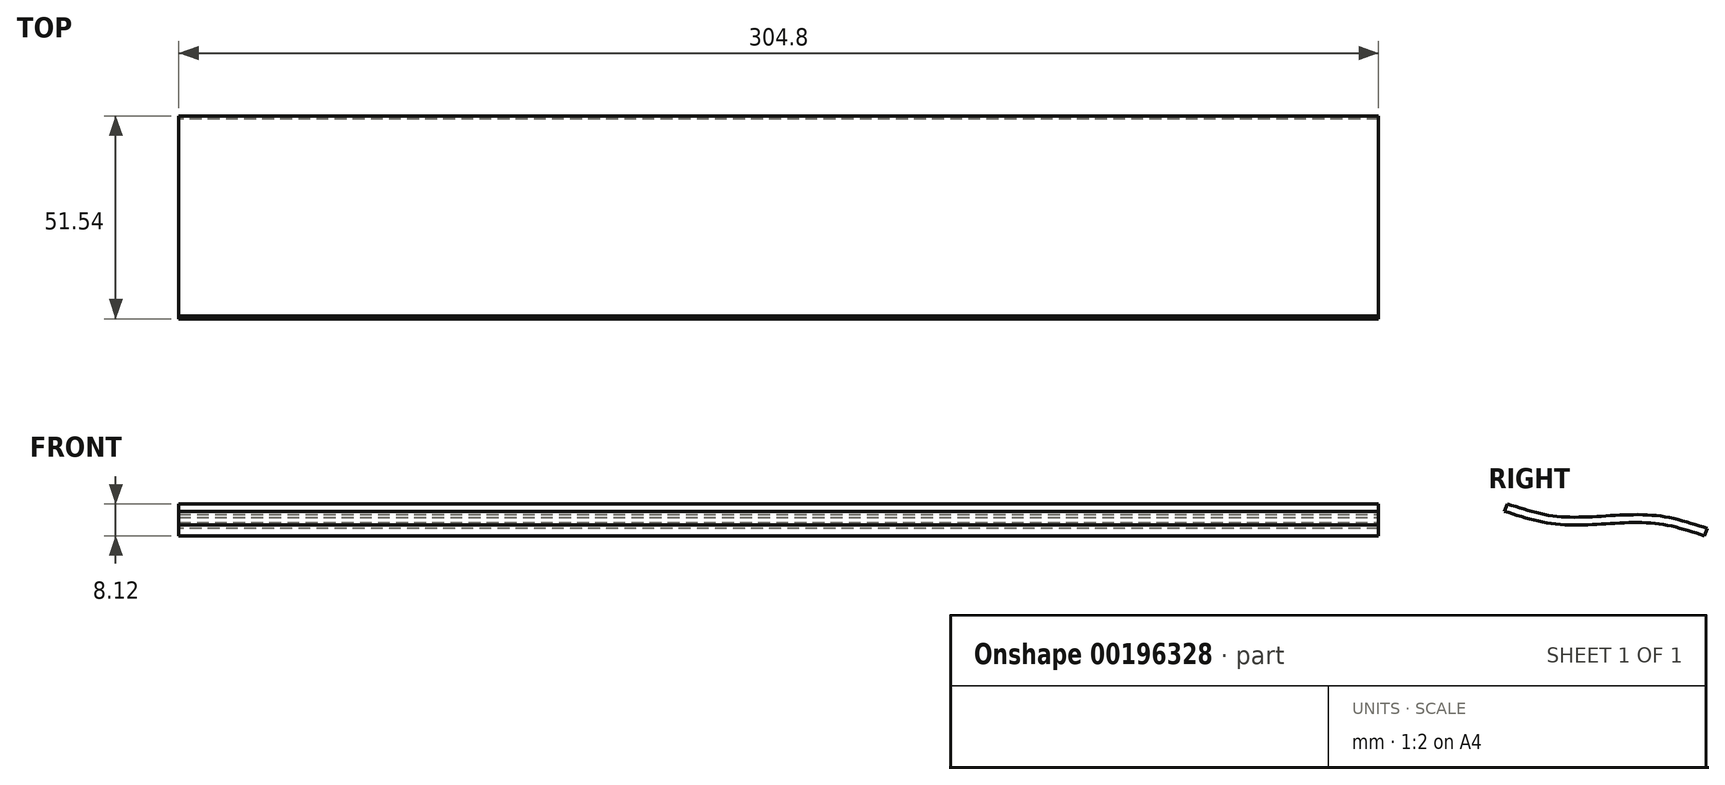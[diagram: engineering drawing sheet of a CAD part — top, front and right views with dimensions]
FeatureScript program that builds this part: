
annotation { "Feature Type Name" : "Feature", "Feature Type Description" : "" }
export const myFeature = defineFeature(function(context is Context, id is Id, definition is map)
    precondition{}
    {
        {
            var Q0;
            Q0=qCreatedBy(makeId("Front.planeOp"),FACE);
            var sketch = newSketch(context, id + "F0", { "sketchPlane" : qUnion([Q0])});
            skLineSegment(sketch, "E0.bottom", {"start": v(152.4, 1) * mm, "end": v(-152.4, 1) * mm});
            skLineSegment(sketch, "E0.top", {"start": v(152.4, -1) * mm, "end": v(-152.4, -1) * mm});
            skLineSegment(sketch, "E0.left", {"start": v(152.4, 1) * mm, "end": v(152.4, -1) * mm});
            skLineSegment(sketch, "E0.right", {"start": v(-152.4, 1) * mm, "end": v(-152.4, -1) * mm});
            skPoint(sketch, "E0.middle", {"position": v(0, 0) * mm});
            skSolve(sketch);
        }
        {
            var Q0;
            Q0=qCreatedBy(makeId("Right.planeOp"),FACE);
            var sketch = newSketch(context, id + "F1", { "sketchPlane" : qUnion([Q0])});
            skFitSpline(sketch, "E1", {"points": [v(0, 0) * mm, v(-13.38, 0) * mm, v(-25.4, 3.13) * mm], "startDerivative": vector(-26.73, -1.62) * mm, "endDerivative": vector(-24.06, 7.94) * mm});
            skLineSegment(sketch, "E2.MirrorCS", {"start": v(-13.38, 0) * mm, "end": v(-13.38, 0) * mm});
            skFitSpline(sketch, "E3.MirrorCS", {"points": [v(0, 0) * mm, v(13.38, 0) * mm, v(25.4, -3.13) * mm], "startDerivative": vector(26.73, 1.62) * mm, "endDerivative": vector(24.06, -7.94) * mm});
            skSolve(sketch);
        }
        {
            var Q0;
            Q0 = qSketchRegion(id + "F0", true);
            var Q1;
            Q1=sQuery(id+"F1.wireOp",EDGE,"E1");
            sweep(context, id + "F2", {"profiles" : qUnion([Q0]), "path" : qUnion([Q1])});
        }
        {
            var Q0;
            Q0=makeQuery(id+"F2.opSweep","CAP_FACE",FACE,{"disambiguationData":[OSD([sQuery(id+"F0.wireOp",EDGE,"E0.bottom"),sQuery(id+"F0.wireOp",EDGE,"E0.top"),sQuery(id+"F0.wireOp",EDGE,"E0.left"),sQuery(id+"F0.wireOp",EDGE,"E0.right"),sQuery(id+"F1.wireOp",VERTEX,"E1.start")])],"isStart":true});
            var Q1;
            Q1=sQuery(id+"F1.wireOp",EDGE,"E3.MirrorCS");
            sweep(context, id + "F3", {"operationType" : NewBodyOperationType.ADD, "profiles" : qUnion([Q0]), "path" : qUnion([Q1])});
        }
    });
